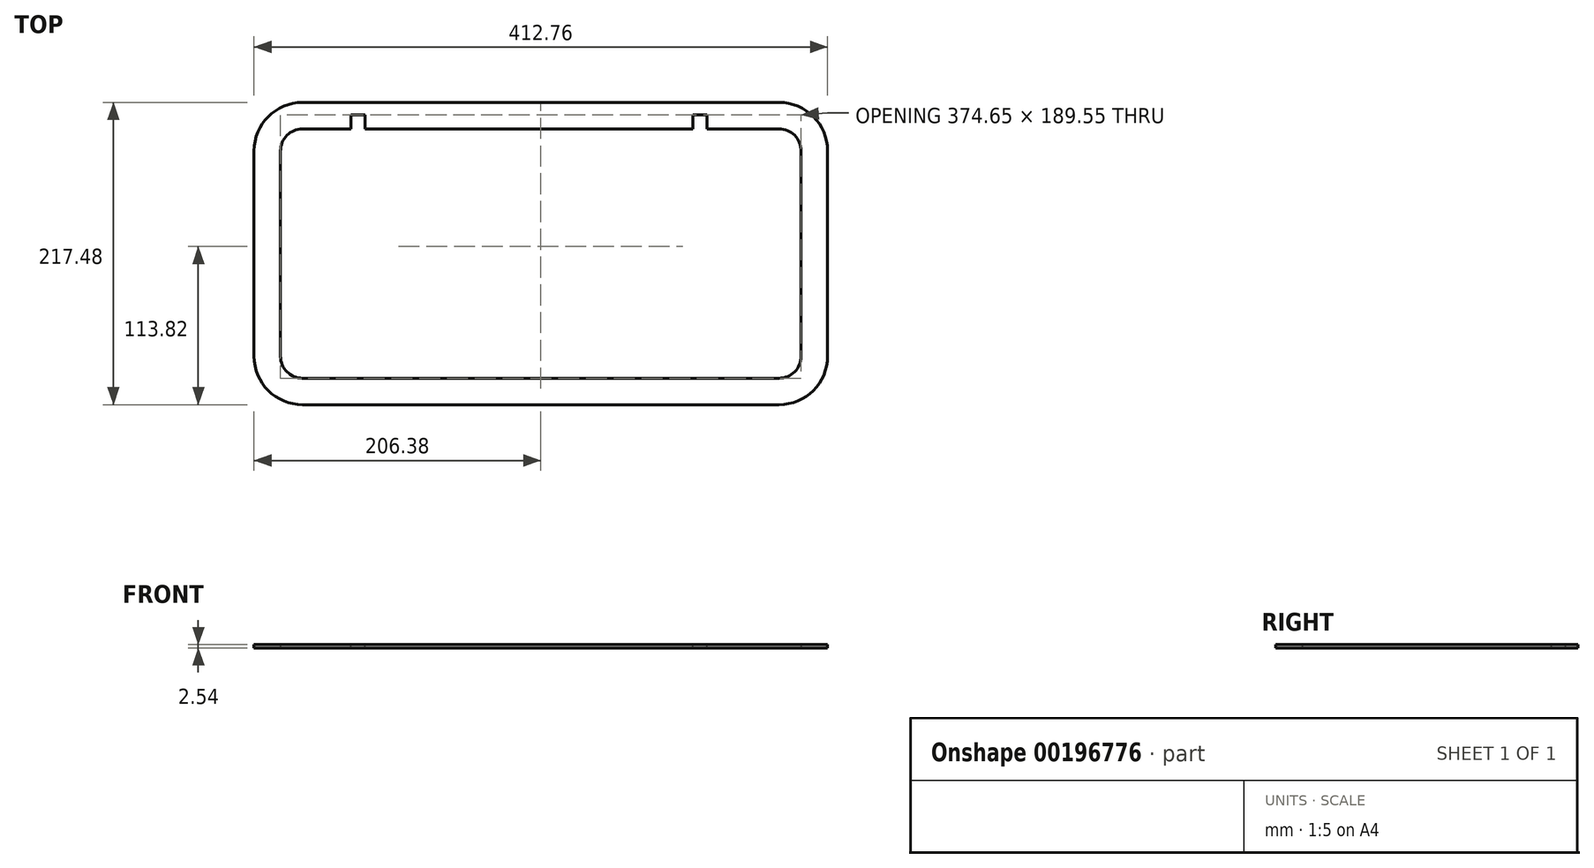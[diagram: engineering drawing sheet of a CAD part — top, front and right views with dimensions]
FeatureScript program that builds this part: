
annotation { "Feature Type Name" : "Feature", "Feature Type Description" : "" }
export const myFeature = defineFeature(function(context is Context, id is Id, definition is map)
    precondition{}
    {
        {
            var Q0;
            Q0=qCreatedBy(makeId("Top.planeOp"),FACE);
            var sketch = newSketch(context, id + "F0", { "sketchPlane" : qUnion([Q0])});
            skLineSegment(sketch, "E0.bottom", {"start": v(171.45, -89.7) * mm, "end": v(-171.45, -89.7) * mm});
            skLineSegment(sketch, "E0.top", {"start": v(171.45, 89.7) * mm, "end": v(-171.45, 89.7) * mm});
            skLineSegment(sketch, "E0.left", {"start": v(187.33, -73.82) * mm, "end": v(187.33, 73.82) * mm});
            skLineSegment(sketch, "E0.right", {"start": v(-187.32, -73.82) * mm, "end": v(-187.33, 73.82) * mm});
            skPoint(sketch, "E0.middle", {"position": v(0, 0) * mm});
            skPoint(sketch, "E1.visualSharp", {"position": v(-187.33, 89.7) * mm});
            skArc(sketch, "E1.filletArc", {"start": v(-171.45, 89.7) * mm, "mid": v(-182.68, 85.04) * mm, "end": v(-187.33, 73.82) * mm});
            skPoint(sketch, "E2.visualSharp", {"position": v(-187.33, -89.7) * mm});
            skArc(sketch, "E2.filletArc", {"start": v(-187.32, -73.82) * mm, "mid": v(-182.68, -85.04) * mm, "end": v(-171.45, -89.7) * mm});
            skPoint(sketch, "E3.visualSharp", {"position": v(187.33, -89.7) * mm});
            skArc(sketch, "E3.filletArc", {"start": v(171.45, -89.7) * mm, "mid": v(182.68, -85.04) * mm, "end": v(187.33, -73.82) * mm});
            skPoint(sketch, "E4.visualSharp", {"position": v(187.33, 89.7) * mm});
            skArc(sketch, "E4.filletArc", {"start": v(187.33, 73.82) * mm, "mid": v(182.68, 85.04) * mm, "end": v(171.45, 89.7) * mm});
            skArc(sketch, "E5.0", {"start": v(206.38, 73.82) * mm, "mid": v(196.15, 98.51) * mm, "end": v(171.45, 108.74) * mm});
            skLineSegment(sketch, "E5.1", {"start": v(206.38, -73.82) * mm, "end": v(206.38, 73.82) * mm});
            skLineSegment(sketch, "E5.2", {"start": v(171.45, 108.74) * mm, "end": v(-171.45, 108.74) * mm});
            skArc(sketch, "E5.3", {"start": v(171.45, -108.74) * mm, "mid": v(196.15, -98.51) * mm, "end": v(206.38, -73.82) * mm});
            skArc(sketch, "E5.4", {"start": v(-171.45, 108.74) * mm, "mid": v(-196.15, 98.51) * mm, "end": v(-206.38, 73.82) * mm});
            skLineSegment(sketch, "E5.5", {"start": v(-206.38, -73.82) * mm, "end": v(-206.38, 73.82) * mm});
            skArc(sketch, "E5.6", {"start": v(-206.37, -73.82) * mm, "mid": v(-196.15, -98.51) * mm, "end": v(-171.45, -108.74) * mm});
            skLineSegment(sketch, "E5.7", {"start": v(171.45, -108.74) * mm, "end": v(-171.45, -108.74) * mm});
            skSolve(sketch);
        }
        {
            var Q0;
            Q0 = qSketchRegion(id + "F0", true);
            extrude(context, id + "F1", {"entities" : qUnion([Q0]), "depth" : 2.54 * mm});
        }
        {
            var Q0;
            Q0=makeQuery(id+"F1.opExtrude","CAP_FACE",FACE,{"disambiguationData":[OSD([sQuery(id+"F0.wireOp",EDGE,"E0.bottom"),sQuery(id+"F0.wireOp",EDGE,"E0.top"),sQuery(id+"F0.wireOp",EDGE,"E0.left"),sQuery(id+"F0.wireOp",EDGE,"E0.right"),sQuery(id+"F0.wireOp",EDGE,"E1.filletArc"),sQuery(id+"F0.wireOp",EDGE,"E2.filletArc"),sQuery(id+"F0.wireOp",EDGE,"E3.filletArc"),sQuery(id+"F0.wireOp",EDGE,"E4.filletArc"),sQuery(id+"F0.wireOp",EDGE,"E5.0"),sQuery(id+"F0.wireOp",EDGE,"E5.1"),sQuery(id+"F0.wireOp",EDGE,"E5.2"),sQuery(id+"F0.wireOp",EDGE,"E5.3"),sQuery(id+"F0.wireOp",EDGE,"E5.4"),sQuery(id+"F0.wireOp",EDGE,"E5.5"),sQuery(id+"F0.wireOp",EDGE,"E5.6"),sQuery(id+"F0.wireOp",EDGE,"E5.7")])],"isStart":false});
            var sketch = newSketch(context, id + "F2", { "sketchPlane" : qUnion([Q0])});
            skLineSegment(sketch, "E6.bottom", {"start": v(-136.53, 89.7) * mm, "end": v(-126.37, 89.7) * mm});
            skLineSegment(sketch, "E6.top", {"start": v(-136.53, 99.85) * mm, "end": v(-126.37, 99.85) * mm});
            skLineSegment(sketch, "E6.left", {"start": v(-136.53, 89.7) * mm, "end": v(-136.53, 99.85) * mm});
            skLineSegment(sketch, "E6.right", {"start": v(-126.37, 89.7) * mm, "end": v(-126.37, 99.85) * mm});
            skLineSegment(sketch, "E7.bottom", {"start": v(109.54, 89.7) * mm, "end": v(119.7, 89.7) * mm});
            skLineSegment(sketch, "E7.top", {"start": v(109.54, 99.85) * mm, "end": v(119.7, 99.85) * mm});
            skLineSegment(sketch, "E7.left", {"start": v(109.54, 89.7) * mm, "end": v(109.54, 99.85) * mm});
            skLineSegment(sketch, "E7.right", {"start": v(119.7, 89.7) * mm, "end": v(119.7, 99.85) * mm});
            skSolve(sketch);
        }
        {
            var Q0;
            Q0 = qSketchRegion(id + "F2", true);
            extrude(context, id + "F3", {"entities" : qUnion([Q0]), "operationType" : NewBodyOperationType.REMOVE, "endBound" : BoundingType.UP_TO_NEXT, "oppositeDirection" : true, "depth" : 25.4 * mm});
        }
    });
